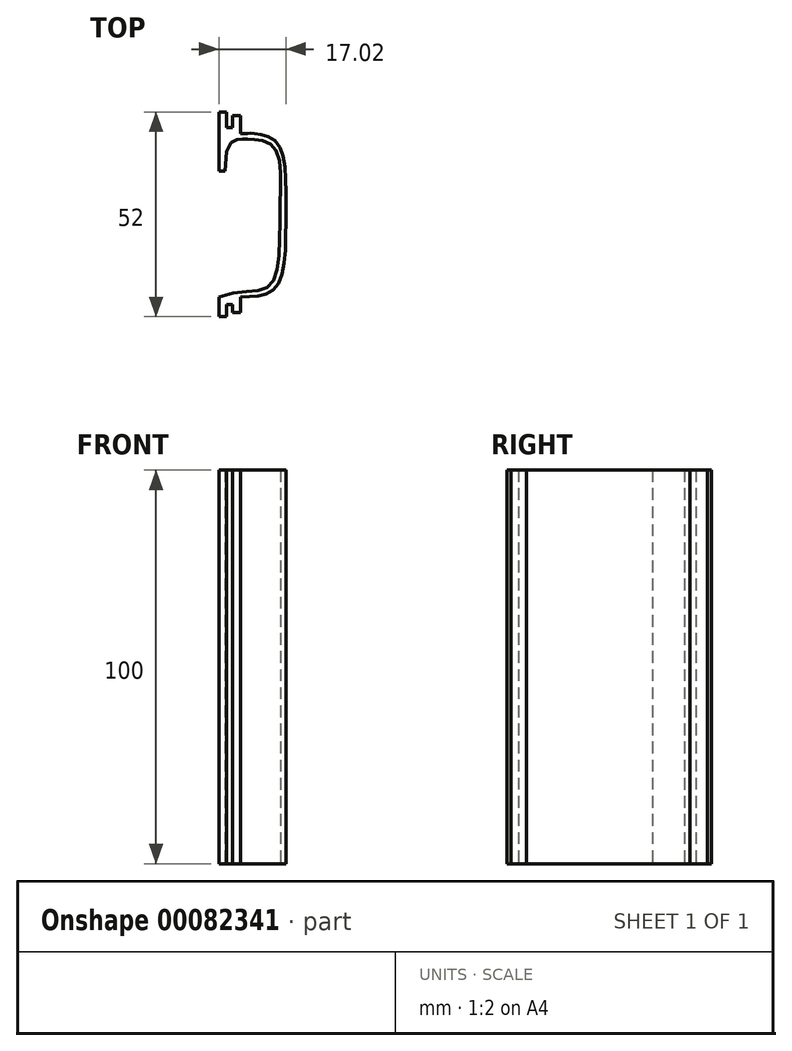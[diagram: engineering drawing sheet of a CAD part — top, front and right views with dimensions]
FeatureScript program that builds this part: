
annotation { "Feature Type Name" : "Feature", "Feature Type Description" : "" }
export const myFeature = defineFeature(function(context is Context, id is Id, definition is map)
    precondition{}
    {
        {
            var Q0;
            Q0=qCreatedBy(makeId("Top.planeOp"),FACE);
            var sketch = newSketch(context, id + "F0", { "sketchPlane" : qUnion([Q0])});
            skLineSegment(sketch, "E0", {"start": v(0, 100.37) * mm, "end": v(0, 85.37) * mm});
            skLineSegment(sketch, "E1", {"start": v(0, 85.37) * mm, "end": v(1.5, 85.37) * mm});
            skLineSegment(sketch, "E2", {"start": v(0, 100.37) * mm, "end": v(2, 100.37) * mm});
            skLineSegment(sketch, "E3", {"start": v(2, 100.37) * mm, "end": v(2, 96.37) * mm});
            skLineSegment(sketch, "E4", {"start": v(2, 96.37) * mm, "end": v(3.5, 96.37) * mm});
            skLineSegment(sketch, "E5", {"start": v(3.5, 96.37) * mm, "end": v(3.5, 99.37) * mm});
            skLineSegment(sketch, "E6", {"start": v(3.5, 99.37) * mm, "end": v(5.5, 99.37) * mm});
            skLineSegment(sketch, "E7", {"start": v(5.5, 99.37) * mm, "end": v(5.5, 94.9) * mm});
            skPoint(sketch, "E8.2.internal.snap0", {"position": v(0, 92.87) * mm});
            skFitSpline(sketch, "E8", {"points": [v(5.5, 94.9) * mm, v(8.42, 94.9) * mm, v(14.4, 92.87) * mm, v(17, 75.79) * mm, v(14.31, 55.68) * mm, v(5.5, 53.37) * mm], "startDerivative": vector(59.88, 0) * mm, "endDerivative": vector(-50.96, -1.54) * mm});
            skFitSpline(sketch, "E9", {"points": [v(1.5, 85.37) * mm, v(5.5, 93.4) * mm, v(8.23, 93.42) * mm, v(13.94, 91.44) * mm, v(15.5, 74.99) * mm, v(12.93, 56.27) * mm, v(0, 53.37) * mm], "startDerivative": vector(-2.04, 148.64) * mm, "endDerivative": vector(-85.68, -32.95) * mm});
            skLineSegment(sketch, "E10", {"start": v(0, 53.37) * mm, "end": v(0, 48.37) * mm});
            skLineSegment(sketch, "E11", {"start": v(0, 48.37) * mm, "end": v(2, 48.37) * mm});
            skLineSegment(sketch, "E12", {"start": v(2, 48.37) * mm, "end": v(2, 51.37) * mm});
            skLineSegment(sketch, "E13", {"start": v(2, 51.37) * mm, "end": v(3.5, 51.37) * mm});
            skLineSegment(sketch, "E14", {"start": v(3.5, 51.37) * mm, "end": v(3.5, 49.37) * mm});
            skLineSegment(sketch, "E15", {"start": v(3.5, 49.37) * mm, "end": v(5.5, 49.37) * mm});
            skLineSegment(sketch, "E16", {"start": v(5.5, 49.37) * mm, "end": v(5.5, 53.37) * mm});
            skSolve(sketch);
        }
        {
            var Q0;
            Q0=makeQuery(id+"F0.imprint","IMPRINT",FACE,{"disambiguationData":[TD([[makeQuery(id+"F0.imprint","IMPRINT",EDGE,{"derivedFrom":sQuery(id+"F0.wireOp",EDGE,"E0")}),1.0]])]});
            extrude(context, id + "F1", {"entities" : qUnion([Q0]), "depth" : 100 * mm});
        }
    });
